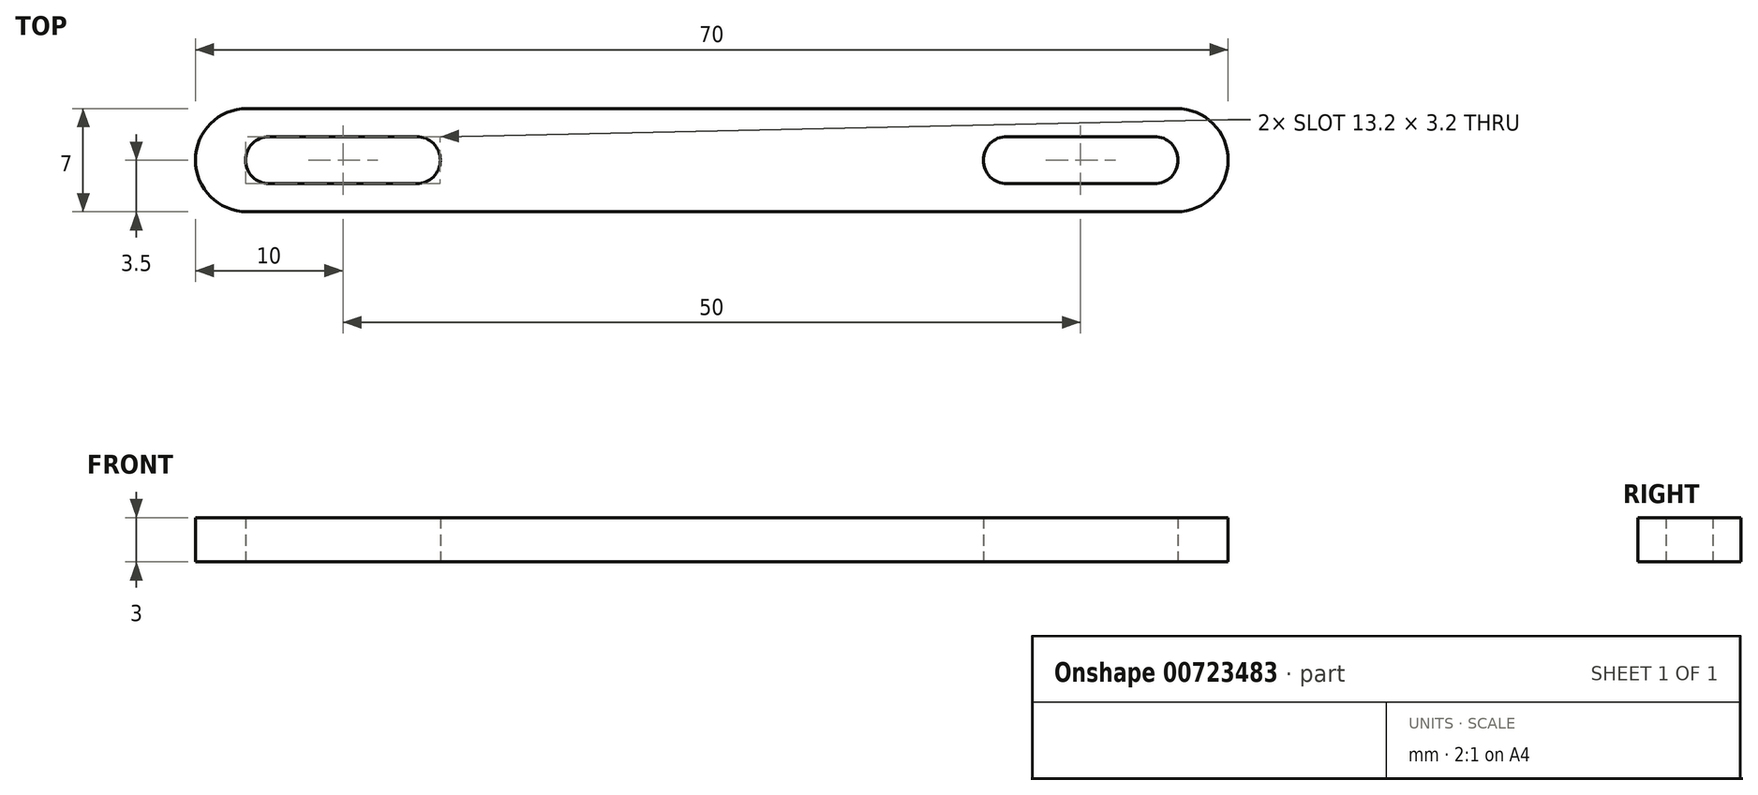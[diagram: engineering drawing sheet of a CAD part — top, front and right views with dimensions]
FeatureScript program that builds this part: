
annotation { "Feature Type Name" : "Feature", "Feature Type Description" : "" }
export const myFeature = defineFeature(function(context is Context, id is Id, definition is map)
    precondition{}
    {
        {
            var Q0;
            Q0=qCreatedBy(makeId("Top.planeOp"),FACE);
            var sketch = newSketch(context, id + "F0", { "sketchPlane" : qUnion([Q0])});
            skLineSegment(sketch, "E0.bottom", {"start": v(35, 3.5) * mm, "end": v(-35, 3.5) * mm});
            skLineSegment(sketch, "E0.top", {"start": v(35, -3.5) * mm, "end": v(-35, -3.5) * mm});
            skLineSegment(sketch, "E0.left", {"start": v(35, 3.5) * mm, "end": v(35, -3.5) * mm});
            skLineSegment(sketch, "E0.right", {"start": v(-35, 3.5) * mm, "end": v(-35, -3.5) * mm});
            skPoint(sketch, "E0.middle", {"position": v(0, 0) * mm});
            skLineSegment(sketch, "E1", {"start": v(30, 0) * mm, "end": v(20, 0) * mm});
            skLineSegment(sketch, "E2", {"start": v(-30, 0) * mm, "end": v(-20, 0) * mm});
            skArc(sketch, "E3.0.startCap", {"start": v(-30, -1.6) * mm, "mid": v(-31.6, 0) * mm, "end": v(-30, 1.6) * mm});
            skArc(sketch, "E3.0.endCap", {"start": v(-20, 1.6) * mm, "mid": v(-18.4, 0) * mm, "end": v(-20, -1.6) * mm});
            skLineSegment(sketch, "E3.0.left", {"start": v(-30, 1.6) * mm, "end": v(-20, 1.6) * mm});
            skLineSegment(sketch, "E3.0.right", {"start": v(-30, -1.6) * mm, "end": v(-20, -1.6) * mm});
            skArc(sketch, "E4.0.startCap", {"start": v(30, 1.6) * mm, "mid": v(31.6, 0) * mm, "end": v(30, -1.6) * mm});
            skArc(sketch, "E4.0.endCap", {"start": v(20, -1.6) * mm, "mid": v(18.4, 0) * mm, "end": v(20, 1.6) * mm});
            skLineSegment(sketch, "E4.0.left", {"start": v(30, -1.6) * mm, "end": v(20, -1.6) * mm});
            skLineSegment(sketch, "E4.0.right", {"start": v(30, 1.6) * mm, "end": v(20, 1.6) * mm});
            skSolve(sketch);
        }
        {
            var Q0;
            Q0=makeQuery(id+"F0.imprint","IMPRINT",FACE,{"disambiguationData":[TD([[makeQuery(id+"F0.imprint","IMPRINT",EDGE,{"derivedFrom":sQuery(id+"F0.wireOp",EDGE,"E0.bottom")}),1.0]])]});
            extrude(context, id + "F1", {"entities" : qUnion([Q0]), "depth" : 3 * mm, "offsetDistance" : 25 * mm});
        }
        {
            var Q0;
            Q0=makeQuery(id+"F1.opExtrude","SWEPT_EDGE",EDGE,{"disambiguationData":[OSD([sQuery(id+"F0.wireOp",EDGE,"E0.bottom"),sQuery(id+"F0.wireOp",EDGE,"E0.right")])]});
            var Q1;
            Q1=makeQuery(id+"F1.opExtrude","SWEPT_EDGE",EDGE,{"disambiguationData":[OSD([sQuery(id+"F0.wireOp",EDGE,"E0.top"),sQuery(id+"F0.wireOp",EDGE,"E0.right")])]});
            var Q2;
            Q2=makeQuery(id+"F1.opExtrude","SWEPT_EDGE",EDGE,{"disambiguationData":[OSD([sQuery(id+"F0.wireOp",EDGE,"E0.bottom"),sQuery(id+"F0.wireOp",EDGE,"E0.left")])]});
            var Q3;
            Q3=makeQuery(id+"F1.opExtrude","SWEPT_EDGE",EDGE,{"disambiguationData":[OSD([sQuery(id+"F0.wireOp",EDGE,"E0.top"),sQuery(id+"F0.wireOp",EDGE,"E0.left")])]});
            fillet(context, id + "F2", {"entities" : qUnion([Q0, Q1, Q2, Q3]), "radius" : 3.5 * mm, "tangentPropagation" : true, "allowEdgeOverflow" : false});
        }
    });
